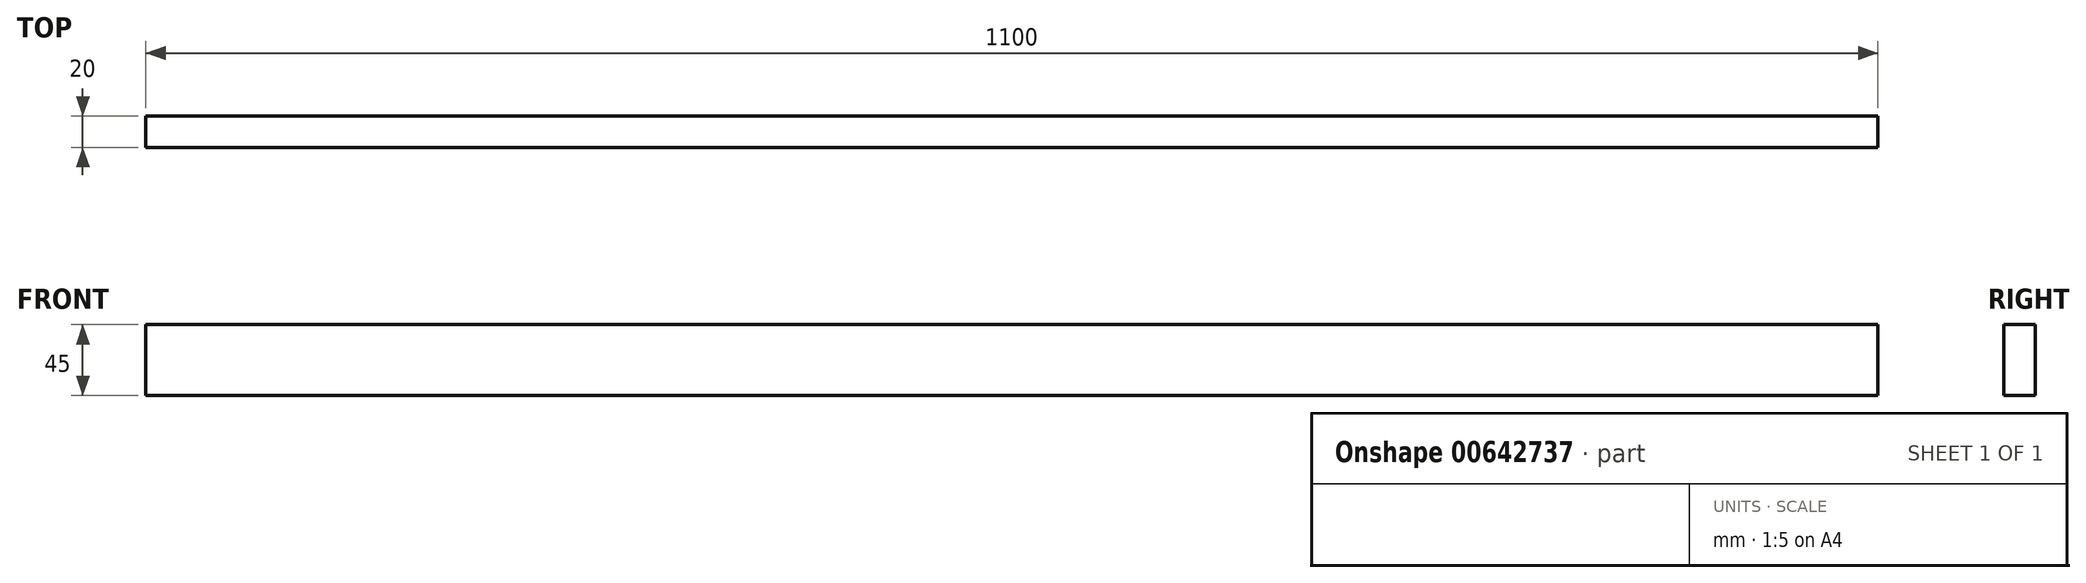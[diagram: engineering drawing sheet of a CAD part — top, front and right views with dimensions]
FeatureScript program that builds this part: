
annotation { "Feature Type Name" : "Feature", "Feature Type Description" : "" }
export const myFeature = defineFeature(function(context is Context, id is Id, definition is map)
    precondition{}
    {
        {
            var Q0;
            Q0=qCreatedBy(makeId("Top.planeOp"),FACE);
            var sketch = newSketch(context, id + "F0", { "sketchPlane" : qUnion([Q0])});
            skLineSegment(sketch, "E0.bottom", {"start": v(0, 0) * mm, "end": v(1100, 0) * mm});
            skLineSegment(sketch, "E0.top", {"start": v(0, 20) * mm, "end": v(1100, 20) * mm});
            skLineSegment(sketch, "E0.left", {"start": v(0, 0) * mm, "end": v(0, 20) * mm});
            skLineSegment(sketch, "E0.right", {"start": v(1100, 0) * mm, "end": v(1100, 20) * mm});
            skSolve(sketch);
        }
        {
            var Q0;
            Q0 = qSketchRegion(id + "F0", true);
            extrude(context, id + "F1", {"entities" : qUnion([Q0]), "depth" : 45 * mm, "offsetDistance" : 25 * mm});
        }
    });
